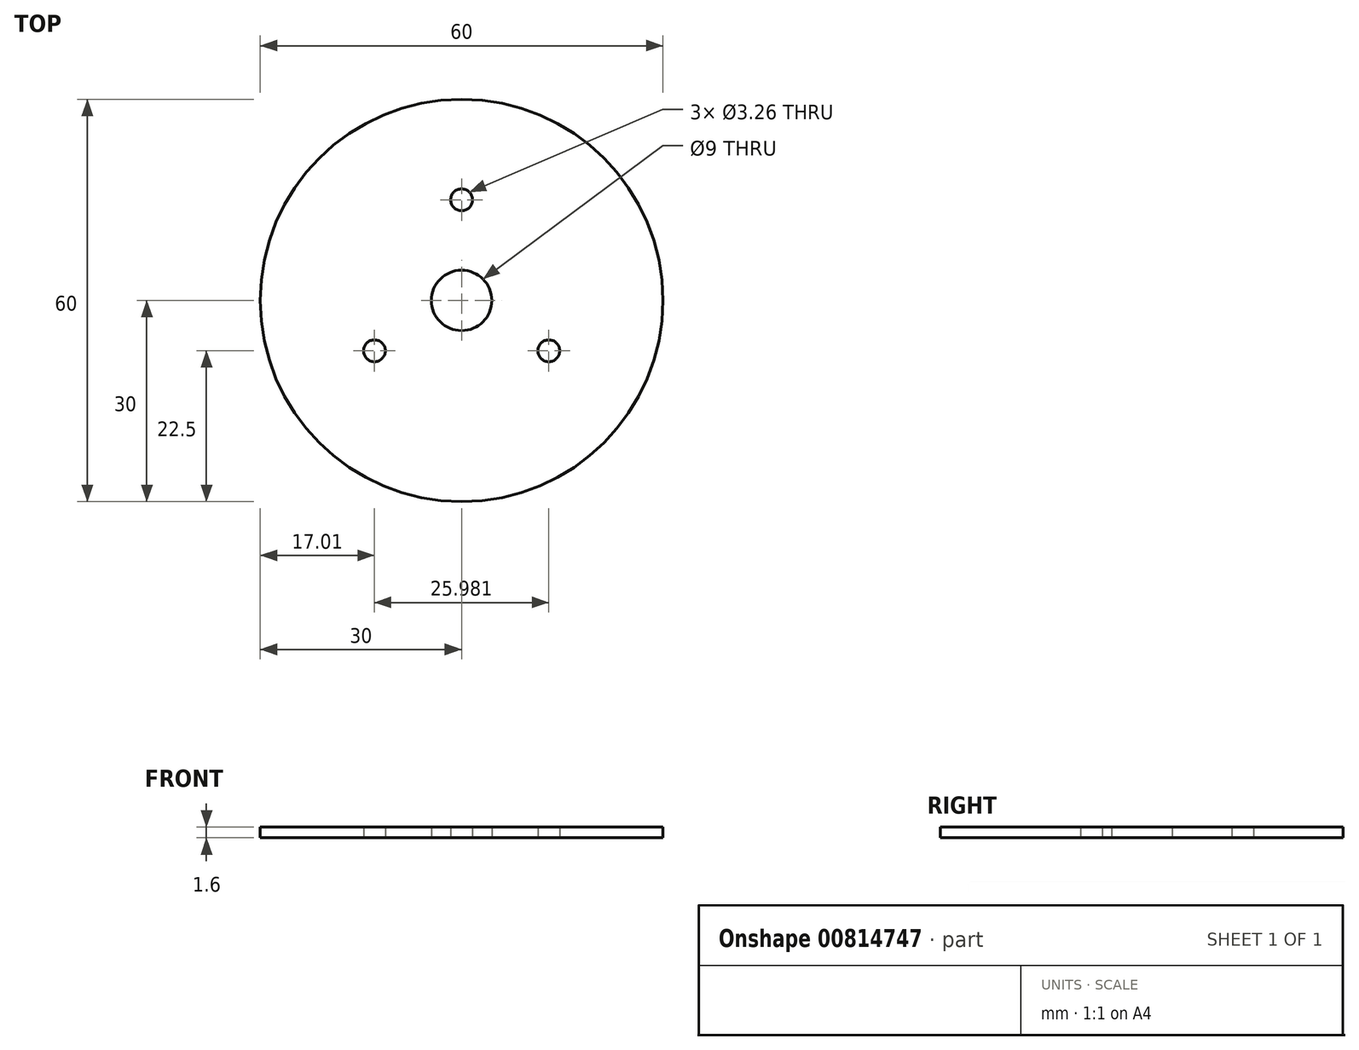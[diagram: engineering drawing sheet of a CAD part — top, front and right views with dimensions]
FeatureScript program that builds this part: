
annotation { "Feature Type Name" : "Feature", "Feature Type Description" : "" }
export const myFeature = defineFeature(function(context is Context, id is Id, definition is map)
    precondition{}
    {
        {
            var Q0;
            Q0=qCreatedBy(makeId("Top.planeOp"),FACE);
            var sketch = newSketch(context, id + "F0", { "sketchPlane" : qUnion([Q0])});
            skCircle(sketch, "E0", {"center": v(0, 0) * mm, "radius": 30 * mm});
            skCircle(sketch, "E1", {"center": v(0, 0) * mm, "radius": 4.5 * mm});
            skCircle(sketch, "E2", {"center": v(0, 15) * mm, "radius": 1.63 * mm});
            skCircle(sketch, "E3.1.0", {"center": v(-13, -7.5) * mm, "radius": 1.63 * mm});
            skCircle(sketch, "E3.2.0", {"center": v(13, -7.5) * mm, "radius": 1.63 * mm});
            skSolve(sketch);
        }
        {
            var Q0;
            Q0 = qSketchRegion(id + "F0", true);
            extrude(context, id + "F1", {"entities" : qUnion([Q0]), "depth" : 1.6 * mm, "offsetDistance" : 25 * mm});
        }
    });
